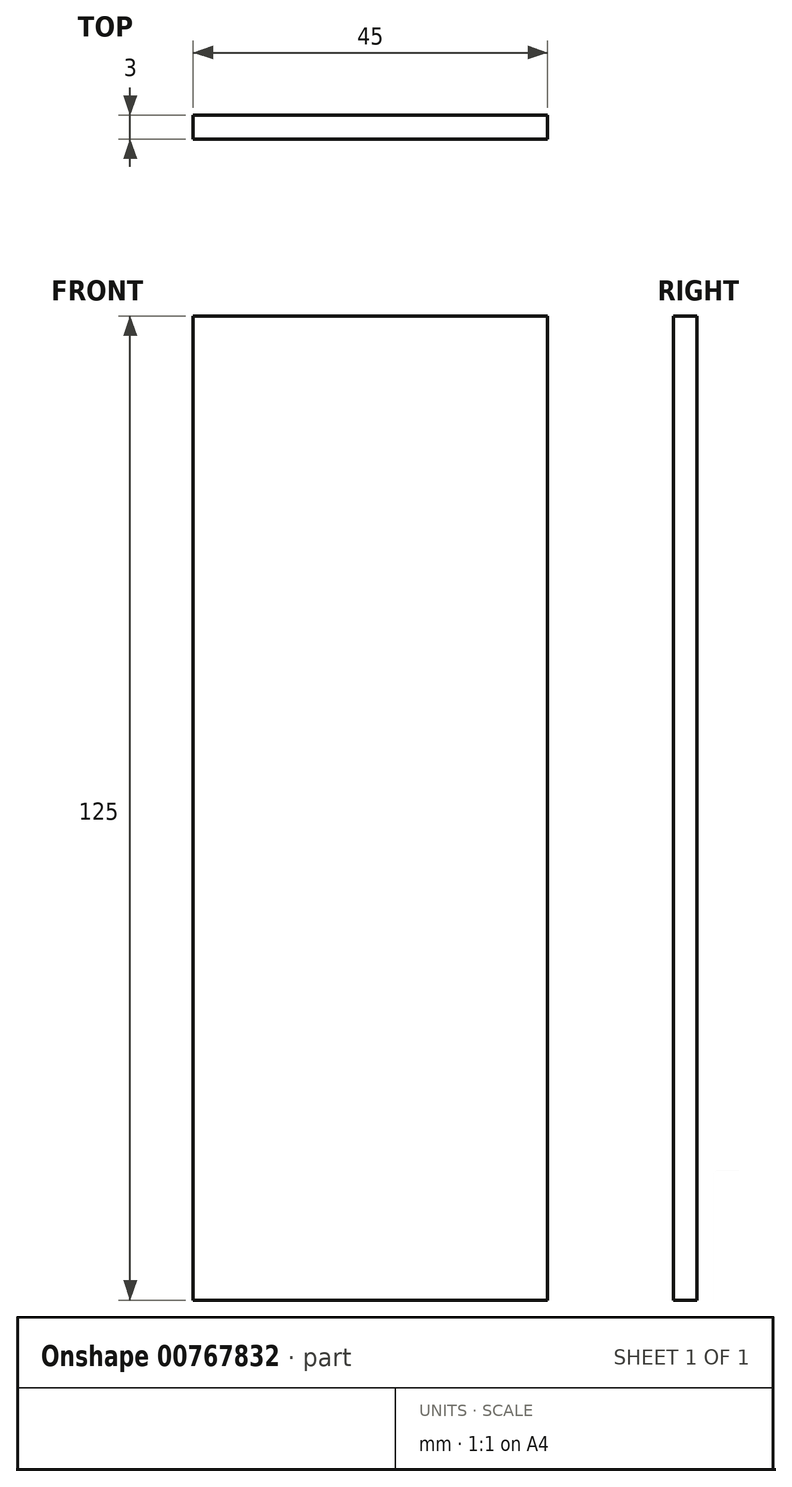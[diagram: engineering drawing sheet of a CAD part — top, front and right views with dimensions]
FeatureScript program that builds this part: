
annotation { "Feature Type Name" : "Feature", "Feature Type Description" : "" }
export const myFeature = defineFeature(function(context is Context, id is Id, definition is map)
    precondition{}
    {
        {
            var Q0;
            Q0=qCreatedBy(makeId("Front.planeOp"),FACE);
            var sketch = newSketch(context, id + "F0", { "sketchPlane" : qUnion([Q0])});
            skLineSegment(sketch, "E0.bottom", {"start": v(21.93, 74.45) * mm, "end": v(66.93, 74.45) * mm});
            skLineSegment(sketch, "E0.top", {"start": v(21.93, -50.55) * mm, "end": v(66.93, -50.55) * mm});
            skLineSegment(sketch, "E0.left", {"start": v(21.93, 74.45) * mm, "end": v(21.93, -50.55) * mm});
            skLineSegment(sketch, "E0.right", {"start": v(66.93, 74.45) * mm, "end": v(66.93, -50.55) * mm});
            skSolve(sketch);
        }
        {
            var Q0;
            Q0 = qSketchRegion(id + "F0", true);
            extrude(context, id + "F1", {"entities" : qUnion([Q0]), "depth" : 3 * mm, "offsetDistance" : 25 * mm});
        }
    });
